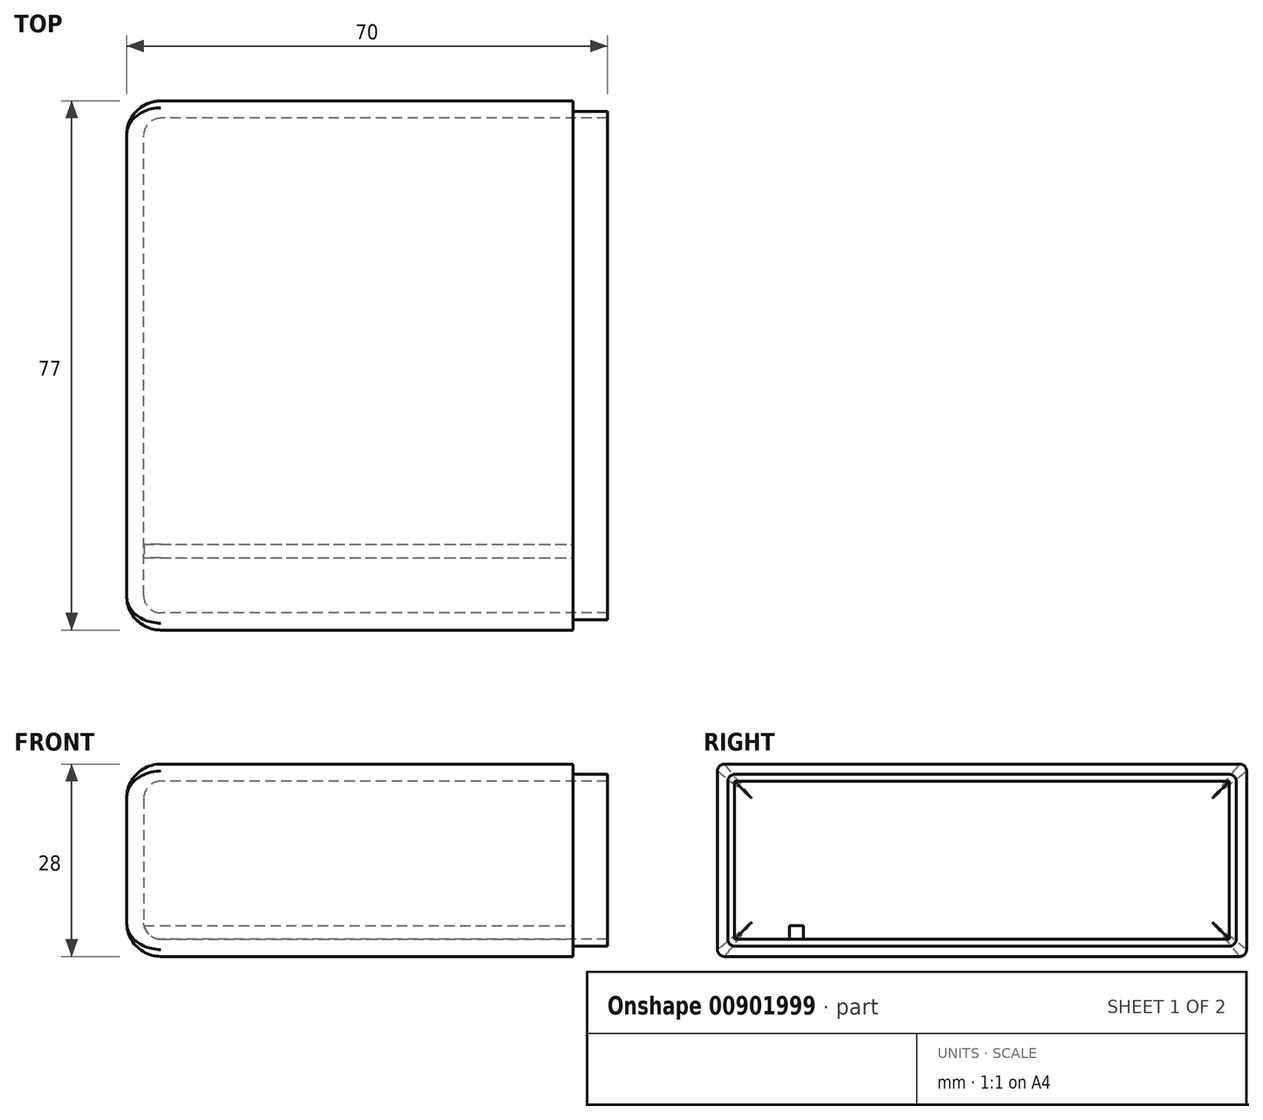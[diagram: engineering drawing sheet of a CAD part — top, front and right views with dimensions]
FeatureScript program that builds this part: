
annotation { "Feature Type Name" : "Feature", "Feature Type Description" : "" }
export const myFeature = defineFeature(function(context is Context, id is Id, definition is map)
    precondition{}
    {
        {
            var Q0;
            Q0=qCreatedBy(makeId("Top.planeOp"),FACE);
            var sketch = newSketch(context, id + "F0", { "sketchPlane" : qUnion([Q0])});
            skLineSegment(sketch, "E0.bottom", {"start": v(-32.5, 38.5) * mm, "end": v(32.5, 38.5) * mm});
            skLineSegment(sketch, "E0.top", {"start": v(-32.5, -38.5) * mm, "end": v(32.5, -38.5) * mm});
            skLineSegment(sketch, "E0.left", {"start": v(-32.5, 38.5) * mm, "end": v(-32.5, -38.5) * mm});
            skLineSegment(sketch, "E0.right", {"start": v(32.5, 38.5) * mm, "end": v(32.5, -38.5) * mm});
            skPoint(sketch, "E0.middle", {"position": v(0, 0) * mm});
            skSolve(sketch);
        }
        {
            var Q0;
            Q0 = qSketchRegion(id + "F0", true);
            extrude(context, id + "F1", {"entities" : qUnion([Q0]), "endBound" : BoundingType.SYMMETRIC, "depth" : 28 * mm, "offsetDistance" : 25 * mm});
        }
        {
            var Q0;
            {var subQ0=sQuery(id+"F0.wireOp",EDGE,"E0.bottom");Q0=makeQuery(id+"F4.opShell","OFFSET_EDGE",EDGE,{"disambiguationData":[OSD([subQ0]),TDD([makeQuery(id+"F1.opExtrude","CAP_EDGE",EDGE,{"disambiguationData":[OSD([subQ0])],"isStart":false})])]});}
            var Q1;
            Q1=makeQuery(id+"F1.opExtrude","CAP_EDGE",EDGE,{"disambiguationData":[OSD([sQuery(id+"F0.wireOp",EDGE,"E0.top")])],"isStart":false});
            var Q2;
            Q2=makeQuery(id+"F1.opExtrude","CAP_EDGE",EDGE,{"disambiguationData":[OSD([sQuery(id+"F0.wireOp",EDGE,"E0.top")])],"isStart":true});
            var Q3;
            Q3=makeQuery(id+"F1.opExtrude","CAP_EDGE",EDGE,{"disambiguationData":[OSD([sQuery(id+"F0.wireOp",EDGE,"E0.bottom")])],"isStart":true});
            var Q4;
            Q4=makeQuery(id+"F1.opExtrude","CAP_EDGE",EDGE,{"disambiguationData":[OSD([sQuery(id+"F0.wireOp",EDGE,"E0.bottom")])],"isStart":false});
            fillet(context, id + "F2", {"entities" : qUnion([Q0, Q1, Q2, Q3, Q4]), "radius" : 1 * mm, "tangentPropagation" : true, "allowEdgeOverflow" : false});
        }
        {
            var Q0;
            Q0=makeQuery(id+"F1.opExtrude","SWEPT_FACE",FACE,{"disambiguationData":[OSD([sQuery(id+"F0.wireOp",EDGE,"E0.left")])]});
            fillet(context, id + "F3", {"entities" : qUnion([Q0]), "radius" : 5 * mm, "tangentPropagation" : true, "allowEdgeOverflow" : false});
        }
        {
            var Q0;
            Q0=makeQuery(id+"F1.opExtrude","SWEPT_FACE",FACE,{"disambiguationData":[OSD([sQuery(id+"F0.wireOp",EDGE,"E0.right")])]});
            shell(context, id + "F4", {"entities" : qUnion([Q0]), "thickness" : 2.5 * mm});
        }
        {
            var Q0;
            {var subQ0=sQuery(id+"F0.wireOp",EDGE,"E0.right");var subQ1=sQuery(id+"F0.wireOp",EDGE,"E0.left");var subQ2=sQuery(id+"F0.wireOp",EDGE,"E0.top");var subQ3=sQuery(id+"F0.wireOp",EDGE,"E0.bottom");Q0=makeQuery(id+"F4.opShell","OFFSET_FACE",FACE,{"disambiguationData":[OSD([subQ3,subQ2,subQ1,subQ0]),TDD([makeQuery(id+"F1.opExtrude","CAP_FACE",FACE,{"disambiguationData":[OSD([subQ3,subQ2,subQ1,subQ0])],"isStart":true})])]});}
            var sketch = newSketch(context, id + "F5", { "sketchPlane" : qUnion([Q0])});
            skLineSegment(sketch, "E1.bottom", {"start": v(-30, -28) * mm, "end": v(32.5, -28) * mm});
            skLineSegment(sketch, "E1.top", {"start": v(-30, -26) * mm, "end": v(32.5, -26) * mm});
            skLineSegment(sketch, "E1.left", {"start": v(-30, -28) * mm, "end": v(-30, -26) * mm});
            skLineSegment(sketch, "E1.right", {"start": v(32.5, -28) * mm, "end": v(32.5, -26) * mm});
            skSolve(sketch);
        }
        {
            var Q0;
            Q0=makeQuery(id+"F5.imprint","IMPRINT",FACE,{"disambiguationData":[TD([[makeQuery(id+"F5.imprint","IMPRINT",EDGE,{"derivedFrom":sQuery(id+"F5.wireOp",EDGE,"E1.bottom")}),1.0]])]});
            extrude(context, id + "F6", {"entities" : qUnion([Q0]), "operationType" : NewBodyOperationType.ADD, "depth" : 2 * mm, "offsetDistance" : 25 * mm});
        }
        {
            var Q0;
            {var subQ0=sQuery(id+"F5.wireOp",EDGE,"E1.right");Q0=makeQuery(id+"FdJKXzpSF2mwR65_1.1.F6.boolean.opBoolean","MERGE",FACE,{"derivedFrom":[makeQuery(id+"F6.boolean.opBoolean","MERGE",FACE,{"derivedFrom":[makeQuery(id+"F1.opExtrude","SWEPT_FACE",FACE,{"disambiguationData":[OSD([sQuery(id+"F0.wireOp",EDGE,"E0.right")])]}),makeQuery(id+"F6.opExtrude","SWEPT_FACE",FACE,{"disambiguationData":[OSD([subQ0])]})]}),makeQuery(id+"FdJKXzpSF2mwR65_1.1.F6.opExtrude","SWEPT_FACE",FACE,{"disambiguationData":[OSD([subQ0])]})]});}
            var sketch = newSketch(context, id + "F7", { "sketchPlane" : qUnion([Q0])});
            skLineSegment(sketch, "E2.bottom", {"start": v(-36, 11.5) * mm, "end": v(36, 11.5) * mm});
            skLineSegment(sketch, "E2.top", {"start": v(-36, -11.5) * mm, "end": v(36, -11.5) * mm});
            skLineSegment(sketch, "E2.left", {"start": v(-36, 11.5) * mm, "end": v(-36, -11.5) * mm});
            skLineSegment(sketch, "E2.right", {"start": v(36, 11.5) * mm, "end": v(36, -11.5) * mm});
            skPoint(sketch, "E2.middle", {"position": v(0, 0) * mm});
            skLineSegment(sketch, "E3.0", {"start": v(-37, 12.5) * mm, "end": v(37, 12.5) * mm});
            skLineSegment(sketch, "E3.1", {"start": v(-37, 12.5) * mm, "end": v(-37, -12.5) * mm});
            skLineSegment(sketch, "E3.2", {"start": v(-37, -12.5) * mm, "end": v(37, -12.5) * mm});
            skLineSegment(sketch, "E3.3", {"start": v(37, 12.5) * mm, "end": v(37, -12.5) * mm});
            skSolve(sketch);
        }
        {
            var Q0;
            Q0 = qSketchRegion(id + "F7", true);
            extrude(context, id + "F8", {"entities" : qUnion([Q0]), "operationType" : NewBodyOperationType.ADD, "depth" : 5 * mm, "offsetDistance" : 25 * mm});
        }
        {
            var Q0;
            Q0=makeQuery(id+"F8.opExtrude","SWEPT_EDGE",EDGE,{"disambiguationData":[OSD([sQuery(id+"F7.wireOp",EDGE,"E3.0"),sQuery(id+"F7.wireOp",EDGE,"E3.1")])]});
            var Q1;
            Q1=makeQuery(id+"F8.opExtrude","SWEPT_EDGE",EDGE,{"disambiguationData":[OSD([sQuery(id+"F7.wireOp",EDGE,"E3.0"),sQuery(id+"F7.wireOp",EDGE,"E3.3")])]});
            var Q2;
            Q2=makeQuery(id+"F8.opExtrude","SWEPT_EDGE",EDGE,{"disambiguationData":[OSD([sQuery(id+"F7.wireOp",EDGE,"E3.2"),sQuery(id+"F7.wireOp",EDGE,"E3.3")])]});
            var Q3;
            Q3=makeQuery(id+"F8.opExtrude","SWEPT_EDGE",EDGE,{"disambiguationData":[OSD([sQuery(id+"F7.wireOp",EDGE,"E3.1"),sQuery(id+"F7.wireOp",EDGE,"E3.2")])]});
            fillet(context, id + "F9", {"entities" : qUnion([Q0, Q1, Q2, Q3]), "radius" : 1 * mm, "tangentPropagation" : true, "allowEdgeOverflow" : false});
        }
    });
